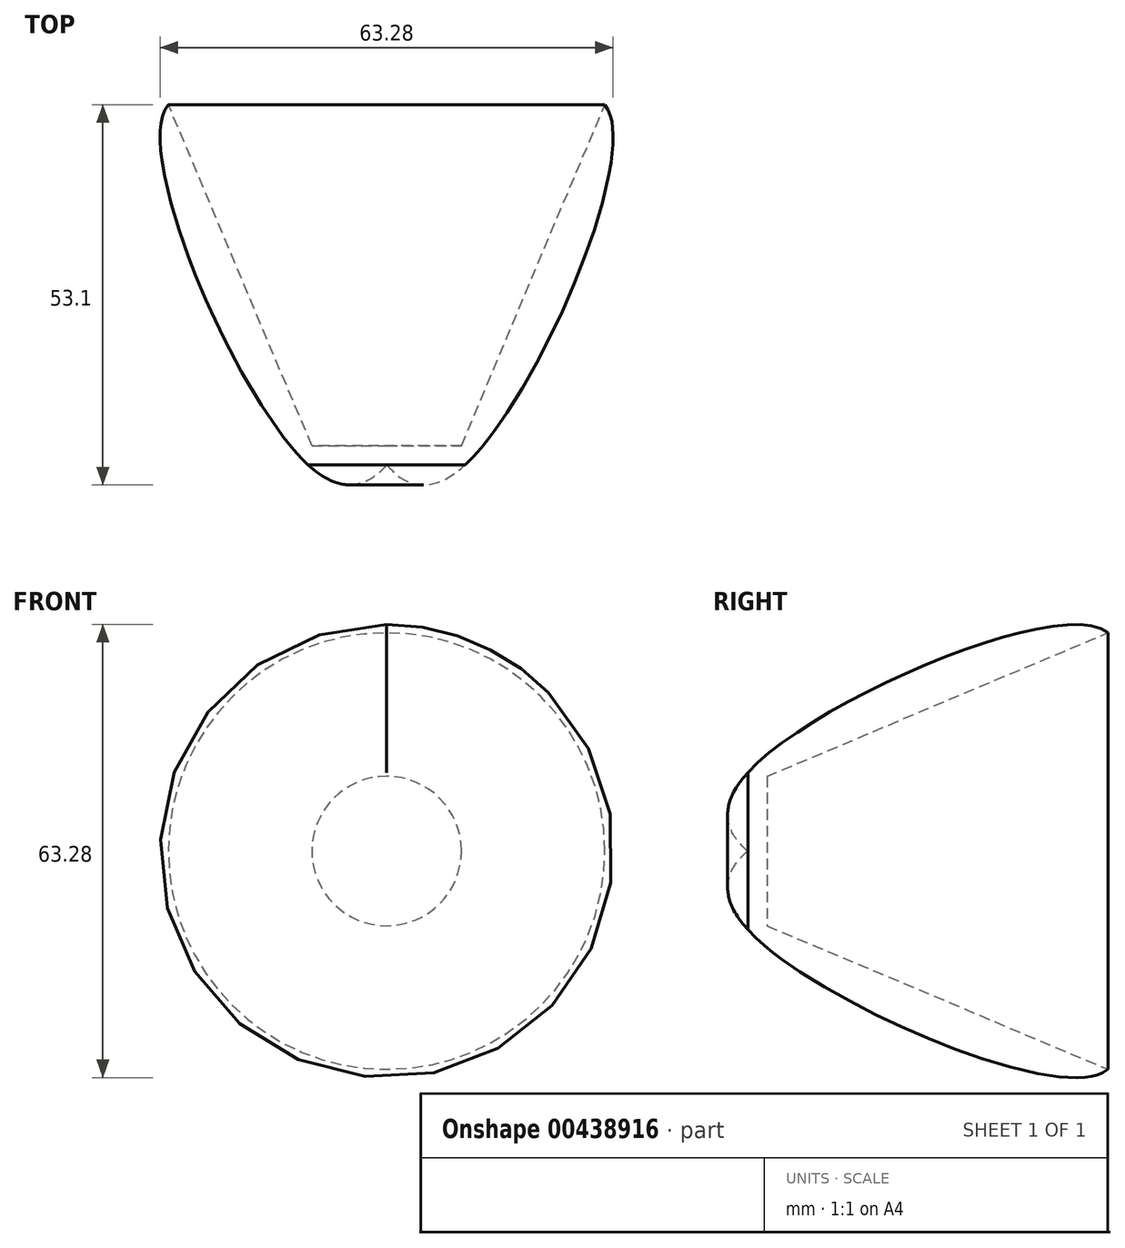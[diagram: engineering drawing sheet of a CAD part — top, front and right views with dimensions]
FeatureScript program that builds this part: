
annotation { "Feature Type Name" : "Feature", "Feature Type Description" : "" }
export const myFeature = defineFeature(function(context is Context, id is Id, definition is map)
    precondition{}
    {
        {
            var Q0;
            Q0=qCreatedBy(makeId("Top.planeOp"),FACE);
            var sketch = newSketch(context, id + "F0", { "sketchPlane" : qUnion([Q0])});
            skLineSegment(sketch, "E0", {"start": v(0, 41.91) * mm, "end": v(0, -34.6) * mm});
            skLineSegment(sketch, "E1", {"start": v(0, 65.99) * mm, "end": v(0, -68.12) * mm});
            skLineSegment(sketch, "E2.bottom", {"start": v(10.97, -28.2) * mm, "end": v(0, -28.2) * mm});
            skLineSegment(sketch, "E2.top", {"start": v(10.97, -34.6) * mm, "end": v(0, -34.6) * mm});
            skLineSegment(sketch, "E2.left", {"start": v(10.97, -28.2) * mm, "end": v(10.97, -34.6) * mm});
            skLineSegment(sketch, "E2.right", {"start": v(0, -28.2) * mm, "end": v(0, -34.6) * mm});
            skFitSpline(sketch, "E3", {"points": [v(0, 0) * mm, v(0, -28.2) * mm, v(10.97, -28.2) * mm, v(30.48, 22.1) * mm, v(0, 0) * mm]});
            skLineSegment(sketch, "E4", {"start": v(30.48, 22.1) * mm, "end": v(10.44, -25.52) * mm});
            skLineSegment(sketch, "E5", {"start": v(10.44, -25.52) * mm, "end": v(0, -25.52) * mm});
            skSolve(sketch);
        }
        {
            var Q0;
            {var subQ0=sQuery(id+"F0.wireOp",EDGE,"E2.bottom");Q0=makeQuery(id+"F0.imprint","IMPRINT",FACE,{"disambiguationData":[TD([[makeQuery(id+"F0.imprint","IMPRINT",EDGE,{"derivedFrom":subQ0}),-1.0]])]});}
            var Q1;
            Q1=makeQuery(id+"F0.imprint","IMPRINT",FACE,{"disambiguationData":[TD([[makeQuery(id+"F0.imprint","IMPRINT",EDGE,{"derivedFrom":sQuery(id+"F0.wireOp",EDGE,"E2.bottom")}),1.0]])]});
            var Q2;
            Q2=sQuery(id+"F0.wireOp",EDGE,"E1");
            revolve(context, id + "F1", {"entities" : qUnion([Q0, Q1]), "axis" : qUnion([Q2]), "revolveType" : RevolveType.FULL});
        }
    });
